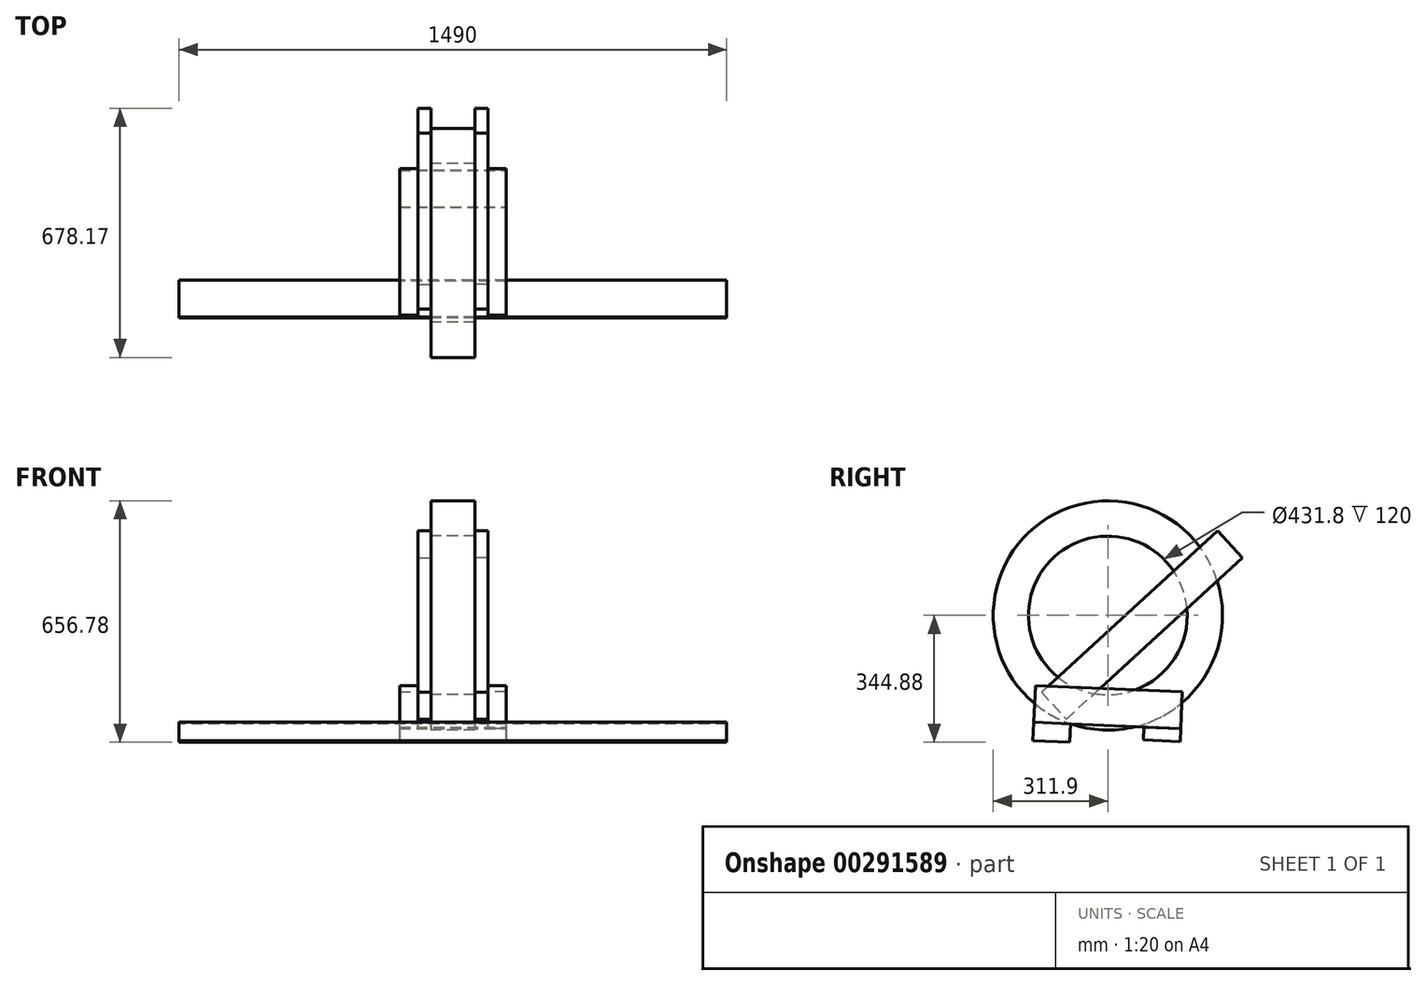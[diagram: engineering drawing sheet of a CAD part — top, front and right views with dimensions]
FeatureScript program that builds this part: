
annotation { "Feature Type Name" : "Feature", "Feature Type Description" : "" }
export const myFeature = defineFeature(function(context is Context, id is Id, definition is map)
    precondition{}
    {
        {
            var Q0;
            Q0=qCreatedBy(makeId("Right.planeOp"),FACE);
            var sketch = newSketch(context, id + "F0", { "sketchPlane" : qUnion([Q0])});
            skCircle(sketch, "E0", {"center": v(0, 0) * mm, "radius": 215.9 * mm});
            skCircle(sketch, "E1", {"center": v(0, 0) * mm, "radius": 311.9 * mm});
            skSolve(sketch);
        }
        {
            var Q0;
            Q0=makeQuery(id+"F0.imprint","IMPRINT",FACE,{"disambiguationData":[TD([[makeQuery(id+"F0.imprint","IMPRINT",EDGE,{"derivedFrom":sQuery(id+"F0.wireOp",EDGE,"E0")}),-1.0]])]});
            extrude(context, id + "F1", {"entities" : qUnion([Q0]), "endBound" : BoundingType.SYMMETRIC, "depth" : 120 * mm});
        }
        {
            var Q0;
            Q0=qCreatedBy(makeId("Right.planeOp"),FACE);
            var sketch = newSketch(context, id + "F2", { "sketchPlane" : qUnion([Q0])});
            skLineSegment(sketch, "E2.bottom", {"start": v(-101.48, -294.93) * mm, "end": v(-201.38, -290.54) * mm});
            skLineSegment(sketch, "E2.top", {"start": v(-103.67, -344.88) * mm, "end": v(-203.58, -340.5) * mm});
            skLineSegment(sketch, "E2.left", {"start": v(-101.48, -294.93) * mm, "end": v(-103.67, -344.88) * mm});
            skLineSegment(sketch, "E2.right", {"start": v(-201.38, -290.54) * mm, "end": v(-203.58, -340.5) * mm});
            skSolve(sketch);
        }
        {
            var Q0;
            Q0=makeQuery(id+"F2.imprint","IMPRINT",FACE,{"disambiguationData":[TD([[makeQuery(id+"F2.imprint","IMPRINT",EDGE,{"derivedFrom":sQuery(id+"F2.wireOp",EDGE,"E2.bottom")}),1.0]])]});
            extrude(context, id + "F3", {"entities" : qUnion([Q0]), "endBound" : BoundingType.SYMMETRIC, "depth" : 1490 * mm});
        }
        {
            var Q0;
            Q0=makeQuery(id+"F1.opExtrude","CAP_FACE",FACE,{"disambiguationData":[OSD([sQuery(id+"F0.wireOp",EDGE,"E0"),sQuery(id+"F0.wireOp",EDGE,"E1")])],"isStart":false});
            var sketch = newSketch(context, id + "F4", { "sketchPlane" : qUnion([Q0])});
            skLineSegment(sketch, "E3", {"start": v(-180.62, -208.51) * mm, "end": v(-113.08, -282.26) * mm});
            skLineSegment(sketch, "E4", {"start": v(-113.08, -282.26) * mm, "end": v(366.27, 156.75) * mm});
            skLineSegment(sketch, "E5", {"start": v(366.27, 156.75) * mm, "end": v(298.73, 230.5) * mm});
            skLineSegment(sketch, "E6", {"start": v(298.73, 230.5) * mm, "end": v(-180.62, -208.51) * mm});
            skSolve(sketch);
        }
        {
            var Q0;
            Q0 = qSketchRegion(id + "F4", true);
            extrude(context, id + "F5", {"entities" : qUnion([Q0]), "depth" : 35 * mm});
        }
        {
            var Q0;
            Q0=makeQuery(id+"F5.opExtrude","SWEPT_BODY",BODY,{"disambiguationData":[OSD([sQuery(id+"F4.wireOp",EDGE,"E3"),sQuery(id+"F4.wireOp",EDGE,"E4"),sQuery(id+"F4.wireOp",EDGE,"E5"),sQuery(id+"F4.wireOp",EDGE,"E6")])]});
            var Q1;
            Q1=qCreatedBy(makeId("Right.planeOp"),FACE);
            mirror(context, id + "F6", {"operationType" : NewBodyOperationType.ADD, "entities" : qUnion([Q0]), "mirrorPlane" : qUnion([Q1])});
        }
        {
            var Q0;
            Q0=makeQuery(id+"F5.opExtrude","CAP_FACE",FACE,{"disambiguationData":[OSD([sQuery(id+"F4.wireOp",EDGE,"E3"),sQuery(id+"F4.wireOp",EDGE,"E4"),sQuery(id+"F4.wireOp",EDGE,"E5"),sQuery(id+"F4.wireOp",EDGE,"E6")])],"isStart":false});
            var sketch = newSketch(context, id + "F7", { "sketchPlane" : qUnion([Q0])});
            skLineSegment(sketch, "E7.0", {"start": v(-101.48, -294.93) * mm, "end": v(-201.38, -290.54) * mm});
            skLineSegment(sketch, "E8", {"start": v(-201.38, -290.54) * mm, "end": v(-197, -190.64) * mm});
            skLineSegment(sketch, "E9", {"start": v(-197, -190.64) * mm, "end": v(202.62, -208.2) * mm});
            skLineSegment(sketch, "E10", {"start": v(202.62, -208.2) * mm, "end": v(198.23, -308.1) * mm});
            skLineSegment(sketch, "E11", {"start": v(-201.38, -290.54) * mm, "end": v(198.23, -308.1) * mm});
            skSolve(sketch);
        }
        {
            var Q0;
            Q0 = qSketchRegion(id + "F7", true);
            extrude(context, id + "F8", {"entities" : qUnion([Q0]), "depth" : 50 * mm});
        }
        {
            var Q0;
            Q0=makeQuery(id+"F8.opExtrude","SWEPT_BODY",BODY,{"disambiguationData":[OSD([sQuery(id+"F7.wireOp",EDGE,"E8"),sQuery(id+"F7.wireOp",EDGE,"E9"),sQuery(id+"F7.wireOp",EDGE,"E10"),sQuery(id+"F7.wireOp",EDGE,"E11")])]});
            var Q1;
            Q1=qCreatedBy(makeId("Right.planeOp"),FACE);
            mirror(context, id + "F9", {"entities" : qUnion([Q0]), "mirrorPlane" : qUnion([Q1])});
        }
        {
            var Q0;
            Q0=makeQuery(id+"F8.opExtrude","CAP_FACE",FACE,{"disambiguationData":[OSD([sQuery(id+"F7.wireOp",EDGE,"E8"),sQuery(id+"F7.wireOp",EDGE,"E9"),sQuery(id+"F7.wireOp",EDGE,"E10"),sQuery(id+"F7.wireOp",EDGE,"E11")])],"isStart":false});
            var sketch = newSketch(context, id + "F10", { "sketchPlane" : qUnion([Q0])});
            skLineSegment(sketch, "E12.0", {"start": v(-201.38, -290.54) * mm, "end": v(198.23, -308.1) * mm});
            skLineSegment(sketch, "E13", {"start": v(198.23, -308.1) * mm, "end": v(196.7, -343.06) * mm});
            skLineSegment(sketch, "E14", {"start": v(196.7, -343.06) * mm, "end": v(96.8, -338.67) * mm});
            skLineSegment(sketch, "E15", {"start": v(96.8, -338.67) * mm, "end": v(98.33, -303.7) * mm});
            skLineSegment(sketch, "E16", {"start": v(98.33, -303.7) * mm, "end": v(198.23, -308.1) * mm});
            skSolve(sketch);
        }
        {
            var Q0;
            Q0=makeQuery(id+"F10.imprint","IMPRINT",FACE,{"disambiguationData":[TD([[makeQuery(id+"F10.imprint","IMPRINT",EDGE,{"derivedFrom":sQuery(id+"F10.wireOp",EDGE,"E13")}),-1.0]])]});
            var Q1;
            Q1=makeQuery(id+"F9.opPattern","COPY",FACE,{"derivedFrom":makeQuery(id+"F8.opExtrude","CAP_FACE",FACE,{"disambiguationData":[OSD([sQuery(id+"F7.wireOp",EDGE,"E8"),sQuery(id+"F7.wireOp",EDGE,"E9"),sQuery(id+"F7.wireOp",EDGE,"E10"),sQuery(id+"F7.wireOp",EDGE,"E11")])],"isStart":false}),"instanceName":"1"});
            extrude(context, id + "F11", {"entities" : qUnion([Q0]), "endBound" : BoundingType.UP_TO_SURFACE, "oppositeDirection" : true, "endBoundEntityFace" : qUnion([Q1]), "depth" : 25 * mm});
        }
    });
